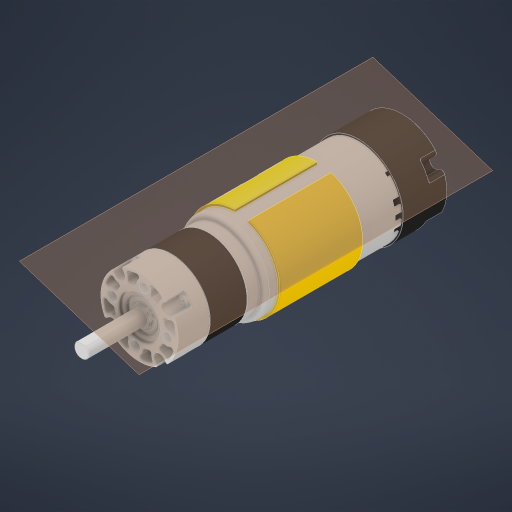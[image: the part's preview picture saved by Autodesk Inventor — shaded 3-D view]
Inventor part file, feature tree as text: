
AUTODESK INVENTOR PART (.ipt)
format: ipt  version: 2023 (Build 270158000, 158)  size: 4,856,832 bytes
history: imported  units: in
note: dims shown in document units (in); Inventor stores cm internally (conversion verified against a paired STEP export)
features: other x2, plane x1, sketch x1, imported_body x1
ambient origin geometry x8: Origin, YZ Plane, XZ Plane, XY Plane, X Axis, Y Axis, Z Axis, Center Point
bodies: Solid1 (imported_parasolid), Solid2 (imported_parasolid), Solid3 (imported_parasolid), Solid4 (imported_parasolid), Solid5 (imported_parasolid), Solid6 (imported_parasolid), Solid7 (imported_parasolid), Solid8 (imported_parasolid), Solid9 (imported_parasolid), Solid10 (imported_parasolid), Solid11 (imported_parasolid), Solid12 (imported_parasolid), Solid13 (imported_parasolid), Solid14 (imported_parasolid), Solid15 (imported_parasolid), Solid16 (imported_parasolid), Solid17 (imported_parasolid), Solid18 (imported_parasolid), Solid19 (imported_parasolid), Solid20 (imported_parasolid), Solid21 (imported_parasolid), Solid22 (imported_parasolid), Solid23 (imported_parasolid), Solid24 (imported_parasolid), Solid25 (imported_parasolid), Solid26 (imported_parasolid), Solid27 (imported_parasolid), Solid28 (imported_parasolid), Solid29 (imported_parasolid), Solid30 (imported_parasolid), Solid31 (imported_parasolid), Solid32 (imported_parasolid), Solid33 (imported_parasolid), Solid34 (imported_parasolid), Solid35 (imported_parasolid), Solid36 (imported_parasolid), Solid37 (imported_parasolid), Solid38 (imported_parasolid), Body1 (imported_parasolid), Body2 (imported_parasolid), Body3 (imported_parasolid), Body4 (imported_parasolid), Body5 (imported_parasolid), Body6 (imported_parasolid), Body7 (imported_parasolid), Body8 (imported_parasolid), Body9 (imported_parasolid), Body10 (imported_parasolid), Body11 (imported_parasolid), Body12 (imported_parasolid), Body13 (imported_parasolid), Body14 (imported_parasolid), Body15 (imported_parasolid), Body16 (imported_parasolid), Body17 (imported_parasolid), Body18 (imported_parasolid), Body19 (imported_parasolid), Body20 (imported_parasolid), Body21 (imported_parasolid), Body22 (imported_parasolid), Body23 (imported_parasolid), Body24 (imported_parasolid), Body25 (imported_parasolid), Body26 (imported_parasolid), Body27 (imported_parasolid), Body28 (imported_parasolid), Body29 (imported_parasolid), Body30 (imported_parasolid), Body31 (imported_parasolid), Body32 (imported_parasolid), Body33 (imported_parasolid), Body34 (imported_parasolid), Body35 (imported_parasolid), Body36 (imported_parasolid), Body37 (imported_parasolid), Body38 (imported_parasolid)
feature tree (5):
  plane  "Work Plane1"
  other  "Decal1"
  sketch  "Sketch1"
  other  "Image1"
  imported_body  NMx_Import_Brep_tag  [imported B-rep: ~144 faces, bbox_mm=None]
